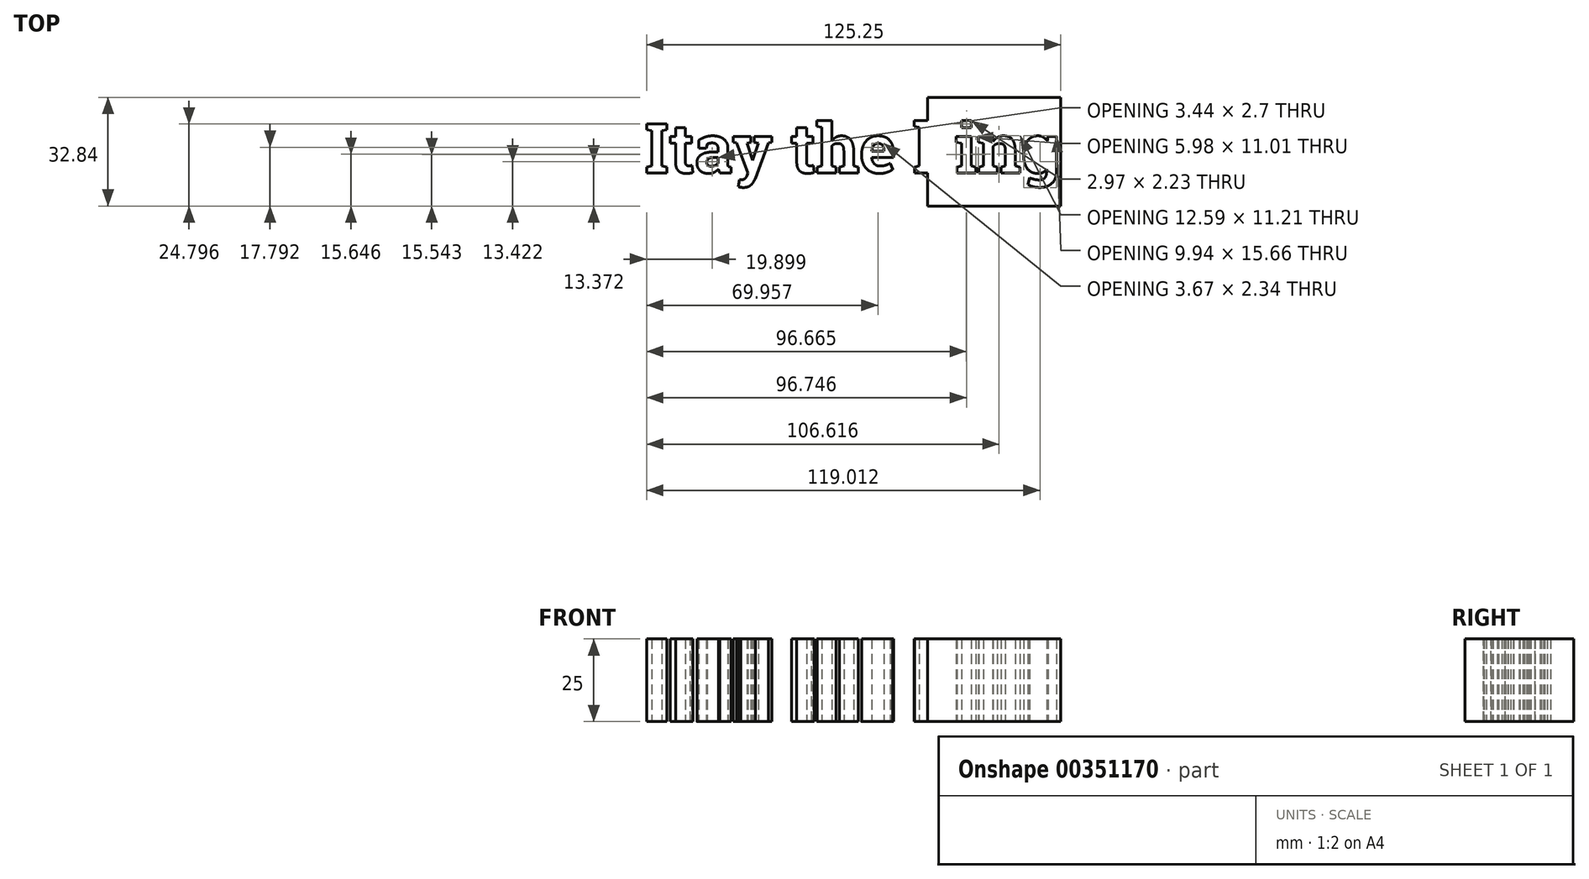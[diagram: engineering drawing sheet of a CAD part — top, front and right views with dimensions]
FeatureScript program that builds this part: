
annotation { "Feature Type Name" : "Feature", "Feature Type Description" : "" }
export const myFeature = defineFeature(function(context is Context, id is Id, definition is map)
    precondition{}
    {
        {
            var Q0;
            Q0=qCreatedBy(makeId("Top.planeOp"),FACE);
            var sketch = newSketch(context, id + "F0", { "sketchPlane" : qUnion([Q0])});
            skLineSegment(sketch, "E0.bottom", {"start": v(0, 0) * mm, "end": v(40.28, 0) * mm});
            skLineSegment(sketch, "E0.top", {"start": v(0, -32.84) * mm, "end": v(40.28, -32.84) * mm});
            skLineSegment(sketch, "E0.left", {"start": v(0, 0) * mm, "end": v(0, -32.84) * mm});
            skLineSegment(sketch, "E0.right", {"start": v(40.28, 0) * mm, "end": v(40.28, -32.84) * mm});
            skText(sketch, "E1", { "text": "Itay the king", "fontName": "RobotoSlab-Bold.ttf"});
            const initialGuessF0  = {"E1": [-0.08553, -0.0228, 1, 0, 0.015]};
            skSetInitialGuess(sketch, initialGuessF0);
            skSolve(sketch);
        }
        {
            var Q0;
            Q0 = qSketchRegion(id + "F0", true);
            extrude(context, id + "F1", {"entities" : qUnion([Q0]), "depth" : 25 * mm});
        }
    });
